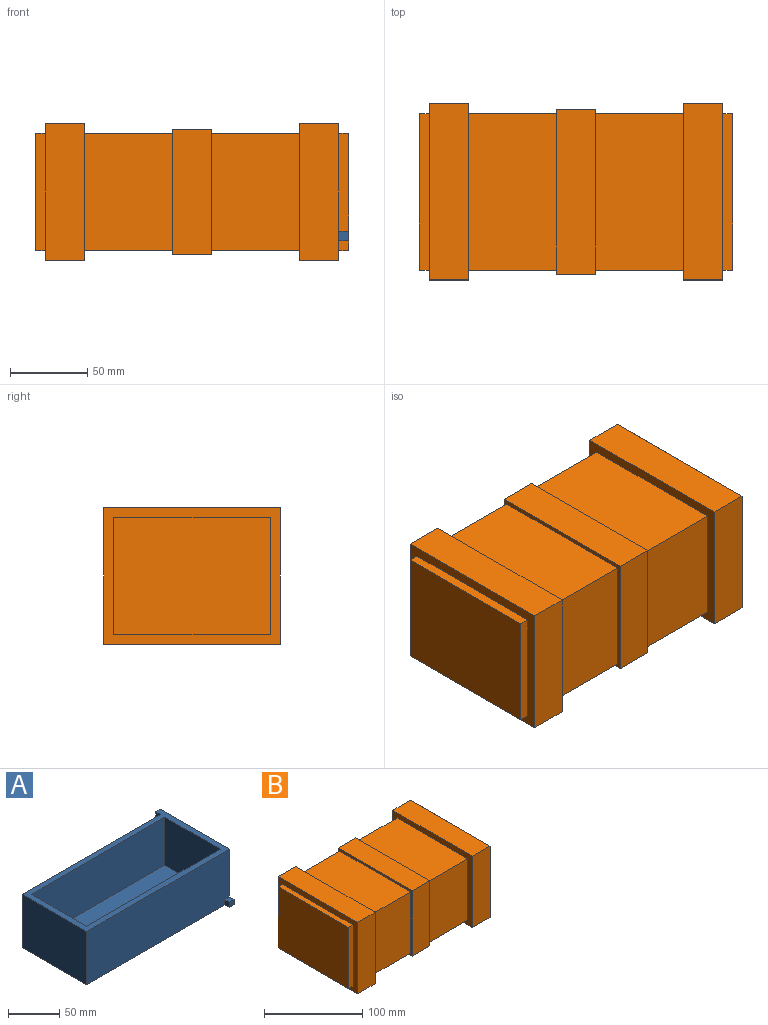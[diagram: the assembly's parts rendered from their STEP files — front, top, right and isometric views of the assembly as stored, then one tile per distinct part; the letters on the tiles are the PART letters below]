
ASSEMBLY  parts=2 mates=1
PART A: 17 faces, bbox 196.9x101.6x63.5 mm
  f0: plane 184.15x76.2mm, normal (0,0,1), area 14032.2mm2, adj f1,f12,f13,f15
  f1: plane 184.15x57.15mm, normal (0,-1,0), area 10524.2mm2, adj f0,f11,f13,f15
  f2: plane 6.35x6.35mm, normal (-1,0,0), area 40.3mm2, adj f3,f4,f11,f14
  f3: plane 6.35x6.35mm, normal (0,1,0), area 40.3mm2, adj f2,f8,f11,f14
  f4: plane 196.85x63.5mm, normal (0,1,0), area 12459.7mm2, adj f2,f8,f10,f11,f14,f16
  f5: plane 196.85x63.5mm, normal (0,-1,0), area 12459.7mm2, adj f6,f8,f9,f10,f11,f16
  f6: plane 6.35x6.35mm, normal (-1,0,0), area 40.3mm2, adj f5,f7,f9,f10
  f7: plane 6.35x6.35mm, normal (0,-1,0), area 40.3mm2, adj f6,f8,f9,f10
  f8: plane 101.6x63.5mm, normal (1,0,0), area 5725.8mm2, adj f3,f4,f5,f7,f9,f10,f11,f14
  f9: plane 6.35x6.35mm, normal (0,0,1), area 40.3mm2, adj f5,f6,f7,f8
  f10: plane 196.85x95.25mm, normal (0,0,-1), area 17540.3mm2, adj f4,f5,f6,f7,f8,f16
  f11: plane 196.85x95.25mm, normal (0,0,1), area 3508.1mm2, adj f1,f2,f3,f4,f5,f8,f12,f13
  f12: plane 184.15x57.15mm, normal (0,1,0), area 10524.2mm2, adj f0,f11,f13,f15
  f13: plane 76.2x57.15mm, normal (-1,0,0), area 4354.8mm2, adj f0,f1,f11,f12
  f14: plane 6.35x6.35mm, normal (0,0,-1), area 40.3mm2, adj f2,f3,f4,f8
  f15: plane 76.2x57.15mm, normal (1,0,0), area 4354.8mm2, adj f0,f1,f11,f12
  f16: plane 88.9x63.5mm, normal (-1,0,0), area 5645.1mm2, adj f4,f5,f10,f11
PART B: 46 faces, bbox 203.2x114.3x88.9 mm
  f0: plane 196.85x63.5mm, normal (0,1,0), area 12459.7mm2, adj f1,f2,f19,f24,f27,f45
  f1: plane 196.85x95.25mm, normal (0,0,1), area 17540.3mm2, adj f0,f12,f18,f22,f24,f45
  f2: plane 196.85x95.25mm, normal (0,0,-1), area 17540.3mm2, adj f0,f7,f18,f19,f24,f45
  f3: plane 76.2x57.15mm, normal (0,1,0), area 4354.8mm2, adj f4,f6,f28,f40
  f4: plane 101.6x57.15mm, normal (0,0,-1), area 5806.4mm2, adj f3,f13,f28,f40
  f5: plane 76.2x57.15mm, normal (0,-1,0), area 4354.8mm2, adj f11,f17,f31,f39
  f6: plane 101.6x57.15mm, normal (0,0,1), area 5806.4mm2, adj f3,f13,f28,f40
  f7: plane 6.35x6.35mm, normal (0,1,0), area 40.3mm2, adj f2,f19,f24,f25
  f8: plane 63.5x6.35mm, normal (0,1,0), area 403.2mm2, adj f10,f22,f24,f26
  f9: plane 76.2x57.15mm, normal (0,1,0), area 4354.8mm2, adj f11,f17,f31,f39
  f10: plane 101.6x6.35mm, normal (0,0,-1), area 645.2mm2, adj f8,f12,f22,f24
  f11: plane 101.6x57.15mm, normal (0,0,-1), area 5806.4mm2, adj f5,f9,f31,f39
  f12: plane 6.35x6.35mm, normal (0,-1,0), area 40.3mm2, adj f1,f10,f22,f24
  f13: plane 76.2x57.15mm, normal (0,-1,0), area 4354.8mm2, adj f4,f6,f28,f40
  f14: plane 76.2x6.35mm, normal (0,-1,0), area 483.9mm2, adj f15,f16,f23,f30
  f15: plane 101.6x76.2mm, normal (-1,0,0), area 7741.9mm2, adj f14,f16,f20,f23
  f16: plane 101.6x6.35mm, normal (0,0,1), area 645.2mm2, adj f14,f15,f20,f30
  f17: plane 101.6x57.15mm, normal (0,0,1), area 5806.4mm2, adj f5,f9,f31,f39
  f18: plane 196.85x63.5mm, normal (0,-1,0), area 12459.7mm2, adj f1,f2,f22,f24,f26,f45
  f19: plane 101.6x63.5mm, normal (1,0,0), area 1008.1mm2, adj f0,f2,f7,f21,f25,f27
  f20: plane 76.2x6.35mm, normal (0,1,0), area 483.9mm2, adj f15,f16,f23,f30
  f21: plane 63.5x6.35mm, normal (0,-1,0), area 403.2mm2, adj f19,f24,f25,f27
  f22: plane 101.6x63.5mm, normal (1,0,0), area 1008.1mm2, adj f1,f8,f10,f12,f18,f26
  f23: plane 101.6x6.35mm, normal (0,0,-1), area 645.2mm2, adj f14,f15,f20,f30
  f24: plane 114.3x88.9mm, normal (1,0,0), area 2500mm2, adj f0,f1,f2,f7,f8,f10,f12,f18
  f25: plane 101.6x6.35mm, normal (0,0,1), area 645.2mm2, adj f7,f19,f21,f24
  f26: plane 6.35x6.35mm, normal (0,0,1), area 40.3mm2, adj f8,f18,f22,f24
  f27: plane 6.35x6.35mm, normal (0,0,-1), area 40.3mm2, adj f0,f19,f21,f24
  f28: plane 114.3x88.9mm, normal (-1,0,0), area 2419.3mm2, adj f3,f4,f6,f13,f29,f34,f36,f38
  f29: plane 114.3x25.4mm, normal (0,0,1), area 2903.2mm2, adj f24,f28,f34,f38
  f30: plane 114.3x88.9mm, normal (-1,0,0), area 2419.3mm2, adj f14,f16,f20,f23,f32,f33,f35,f37
  f31: plane 114.3x88.9mm, normal (1,0,0), area 2419.3mm2, adj f5,f9,f11,f17,f32,f33,f35,f37
  f32: plane 114.3x25.4mm, normal (0,0,1), area 2903.2mm2, adj f30,f31,f33,f37
  f33: plane 88.9x25.4mm, normal (0,-1,0), area 2258.1mm2, adj f30,f31,f32,f35
  f34: plane 88.9x25.4mm, normal (0,-1,0), area 2258.1mm2, adj f24,f28,f29,f36
  f35: plane 114.3x25.4mm, normal (0,0,-1), area 2903.2mm2, adj f30,f31,f33,f37
  f36: plane 114.3x25.4mm, normal (0,0,-1), area 2903.2mm2, adj f24,f28,f34,f38
  f37: plane 88.9x25.4mm, normal (0,1,0), area 2258.1mm2, adj f30,f31,f32,f35
  f38: plane 88.9x25.4mm, normal (0,1,0), area 2258.1mm2, adj f24,f28,f29,f36
  f39: plane 106.68x81.28mm, normal (-1,0,0), area 929mm2, adj f5,f9,f11,f17,f41,f42,f43,f44
  f40: plane 106.68x81.28mm, normal (1,0,0), area 929mm2, adj f3,f4,f6,f13,f41,f42,f43,f44
  f41: plane 106.68x25.4mm, normal (0,0,1), area 2709.7mm2, adj f39,f40,f42,f44
  f42: plane 81.28x25.4mm, normal (0,-1,0), area 2064.5mm2, adj f39,f40,f41,f43
  f43: plane 106.68x25.4mm, normal (0,0,-1), area 2709.7mm2, adj f39,f40,f42,f44
  f44: plane 81.28x25.4mm, normal (0,1,0), area 2064.5mm2, adj f39,f40,f41,f43
  f45: plane 88.9x63.5mm, normal (1,0,0), area 5645.2mm2, adj f0,f1,f2,f18
PLACE A t=(-127.21,-192.78,44.08)mm
PLACE B t=(-137.96,-83.83,37.73)mm
MATE fastened A.f8 <-> B.f19  axis (1,0,0) through (-40.05,-36.67,107.58)mm
